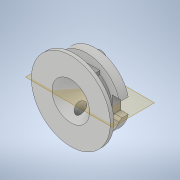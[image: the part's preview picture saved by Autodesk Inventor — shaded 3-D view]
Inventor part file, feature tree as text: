
AUTODESK INVENTOR PART (.ipt)
format: ipt  version: 2020.4 (Build 244396010, 396A)  size: 196,096 bytes
history: native  units: mm
features: extrude x2, sketch x2, plane x1, mirror x1, imported_body x1
ambient origin geometry x8: Origin, YZ Plane, XZ Plane, XY Plane, X Axis, Y Axis, Z Axis, Center Point
bodies: Solid1 (feature_tree)
feature tree (7):
  extrude  "Extrusion1"  Depth=4.2mm
  extrude  "Extrusion2"  Depth=3.0mm TaperAngle=0.0deg
  plane  "Work Plane1"
  mirror  "Mirror1"
  sketch  "Sketch1"  dims[d0=3.5mm d1=4.2mm]
  sketch  "Sketch2"  dims[d2=4.0mm d3=0.0mm d5=3.0mm d6=0.0mm d7=3.5mm d8=2.0mm d4=5.0mm]
  imported_body  "Base1"
